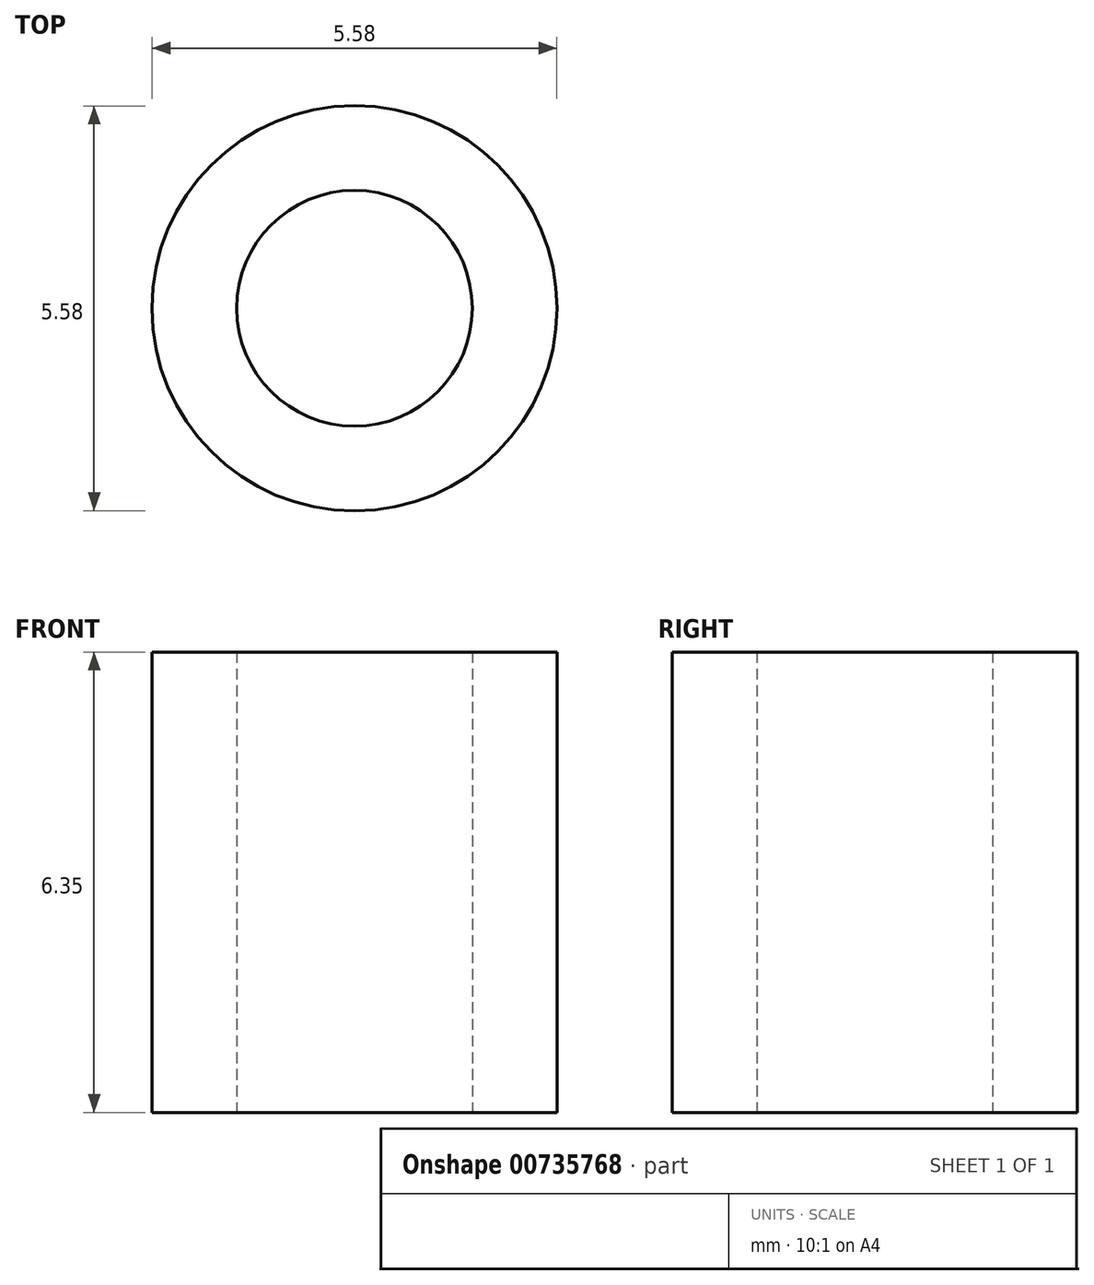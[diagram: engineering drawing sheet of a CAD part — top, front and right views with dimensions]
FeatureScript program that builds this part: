
annotation { "Feature Type Name" : "Feature", "Feature Type Description" : "" }
export const myFeature = defineFeature(function(context is Context, id is Id, definition is map)
    precondition{}
    {
        {
            var Q0;
            Q0=qCreatedBy(makeId("Top.planeOp"),FACE);
            var sketch = newSketch(context, id + "F0", { "sketchPlane" : qUnion([Q0])});
            skCircle(sketch, "E0", {"center": v(0, 0) * mm, "radius": 2.8 * mm});
            skCircle(sketch, "E1", {"center": v(0, 0) * mm, "radius": 1.63 * mm});
            skSolve(sketch);
        }
        {
            var Q0;
            Q0 = qSketchRegion(id + "F0", true);
            extrude(context, id + "F1", {"entities" : qUnion([Q0]), "depth" : 6.35 * mm, "offsetDistance" : 25.4 * mm});
        }
    });
